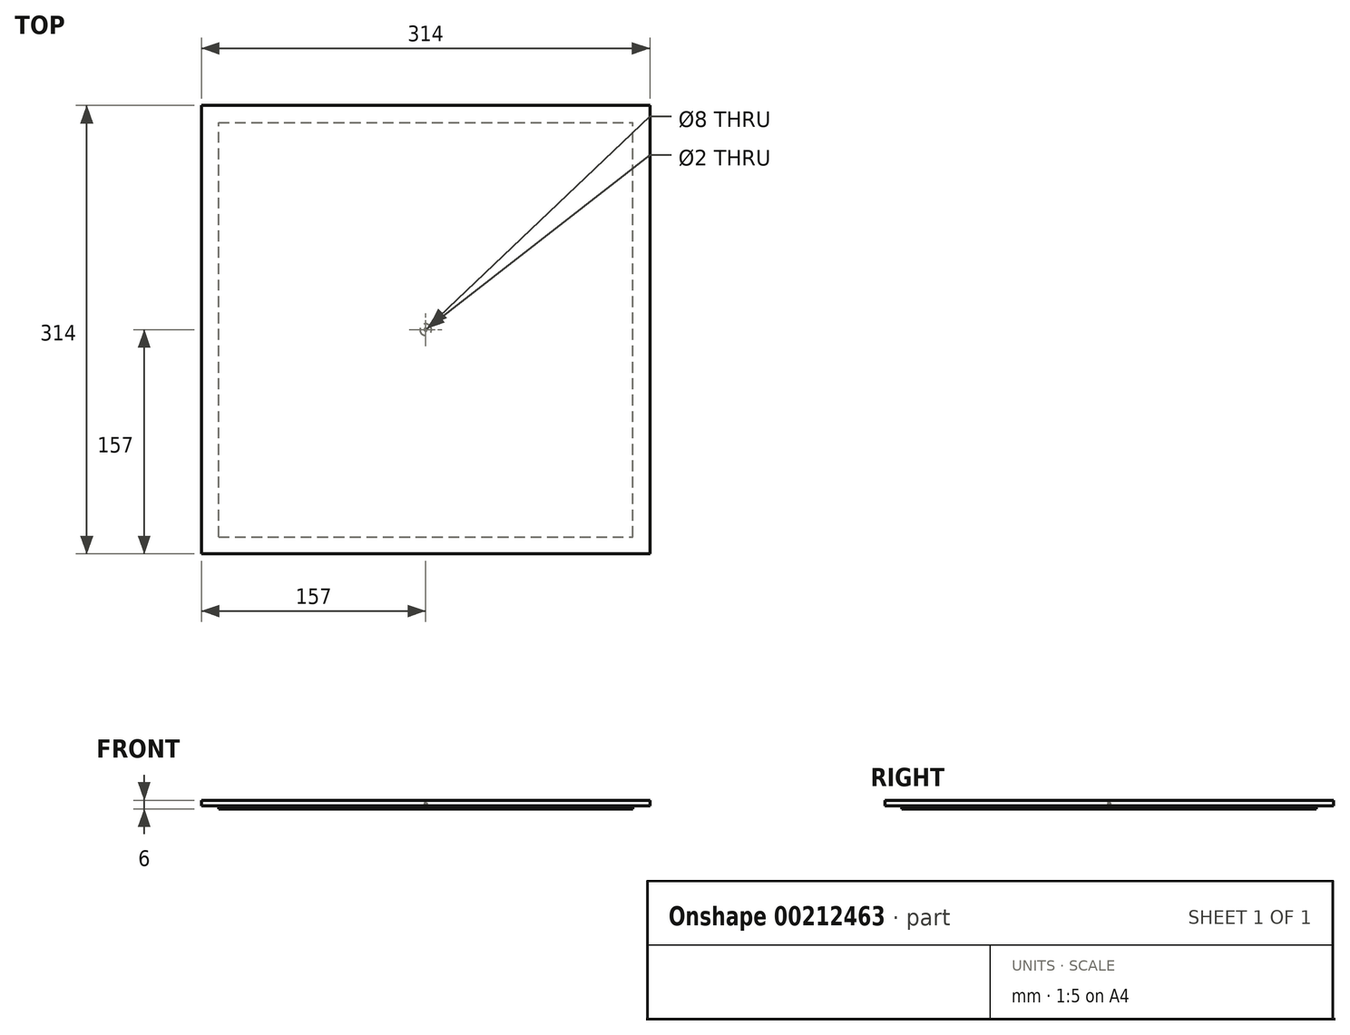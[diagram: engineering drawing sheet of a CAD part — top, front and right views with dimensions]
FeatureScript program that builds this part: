
annotation { "Feature Type Name" : "Feature", "Feature Type Description" : "" }
export const myFeature = defineFeature(function(context is Context, id is Id, definition is map)
    precondition{}
    {
        {
            var Q0;
            Q0=qCreatedBy(makeId("Top.planeOp"),FACE);
            var sketch = newSketch(context, id + "F0", { "sketchPlane" : qUnion([Q0])});
            skLineSegment(sketch, "E0.bottom", {"start": v(-157, 157) * mm, "end": v(157, 157) * mm});
            skLineSegment(sketch, "E0.top", {"start": v(-157, -157) * mm, "end": v(157, -157) * mm});
            skLineSegment(sketch, "E0.left", {"start": v(-157, 157) * mm, "end": v(-157, -157) * mm});
            skLineSegment(sketch, "E0.right", {"start": v(157, 157) * mm, "end": v(157, -157) * mm});
            skPoint(sketch, "E0.middle", {"position": v(0, 0) * mm});
            skLineSegment(sketch, "E1", {"start": v(-149.93, -157) * mm, "end": v(-149.93, -148.45) * mm, "construction": true});
            skLineSegment(sketch, "E2", {"start": v(-157, -148.45) * mm, "end": v(-149.93, -148.45) * mm, "construction": true});
            skSolve(sketch);
        }
        {
            var Q0;
            Q0=makeQuery(id+"F0.imprint","IMPRINT",FACE,{"disambiguationData":[TD([[makeQuery(id+"F0.imprint","IMPRINT",EDGE,{"derivedFrom":sQuery(id+"F0.wireOp",EDGE,"E0.bottom")}),-1.0]])]});
            extrude(context, id + "F1", {"entities" : qUnion([Q0]), "depth" : 4 * mm});
        }
        {
            var Q0;
            Q0=makeQuery(id+"F1.opExtrude","CAP_FACE",FACE,{"disambiguationData":[OSD([sQuery(id+"F0.wireOp",EDGE,"E0.bottom"),sQuery(id+"F0.wireOp",EDGE,"E0.top"),sQuery(id+"F0.wireOp",EDGE,"E0.left"),sQuery(id+"F0.wireOp",EDGE,"E0.right")])],"isStart":true});
            var sketch = newSketch(context, id + "F2", { "sketchPlane" : qUnion([Q0])});
            skPoint(sketch, "E3", {"position": v(0, 0) * mm});
            skCircle(sketch, "E4", {"center": v(0, 0) * mm, "radius": 0.43 * mm});
            skSolve(sketch);
        }
        {
            var Q0;
            Q0=sQuery(id+"F2.wireOp",VERTEX,"E3");
            var Q1;
            Q1=makeQuery(id+"F1.opExtrude","SWEPT_BODY",BODY,{"disambiguationData":[OSD([sQuery(id+"F0.wireOp",EDGE,"E0.bottom"),sQuery(id+"F0.wireOp",EDGE,"E0.top"),sQuery(id+"F0.wireOp",EDGE,"E0.left"),sQuery(id+"F0.wireOp",EDGE,"E0.right")])]});
            hole(context, id + "F3", {"style" : HoleStyle.SIMPLE, "endStyle" : HoleEndStyle.BLIND, "holeDiameter" : 2 * mm, "holeDepth" : 2 * mm, "startFromSketch" : true, "locations" : qUnion([Q0]), "scope" : qUnion([Q1])});
        }
        {
            var Q0;
            Q0=makeQuery(id+"F1.opExtrude","CAP_FACE",FACE,{"disambiguationData":[OSD([sQuery(id+"F0.wireOp",EDGE,"E0.bottom"),sQuery(id+"F0.wireOp",EDGE,"E0.top"),sQuery(id+"F0.wireOp",EDGE,"E0.left"),sQuery(id+"F0.wireOp",EDGE,"E0.right")])],"isStart":true});
            var sketch = newSketch(context, id + "F4", { "sketchPlane" : qUnion([Q0])});
            skLineSegment(sketch, "E5.bottom", {"start": v(-144.96, 145.08) * mm, "end": v(144.96, 145.08) * mm});
            skLineSegment(sketch, "E5.top", {"start": v(-144.96, -145.08) * mm, "end": v(144.96, -145.08) * mm});
            skLineSegment(sketch, "E5.left", {"start": v(-144.96, 145.08) * mm, "end": v(-144.96, -145.08) * mm});
            skLineSegment(sketch, "E5.right", {"start": v(144.96, 145.08) * mm, "end": v(144.96, -145.08) * mm});
            skPoint(sketch, "E5.middle", {"position": v(0, 0) * mm});
            skCircle(sketch, "E6", {"center": v(0, 0) * mm, "radius": 4 * mm});
            skSolve(sketch);
        }
        {
            var Q0;
            Q0 = qSketchRegion(id + "F4", true);
            extrude(context, id + "F5", {"entities" : qUnion([Q0]), "depth" : 2 * mm});
        }
    });
